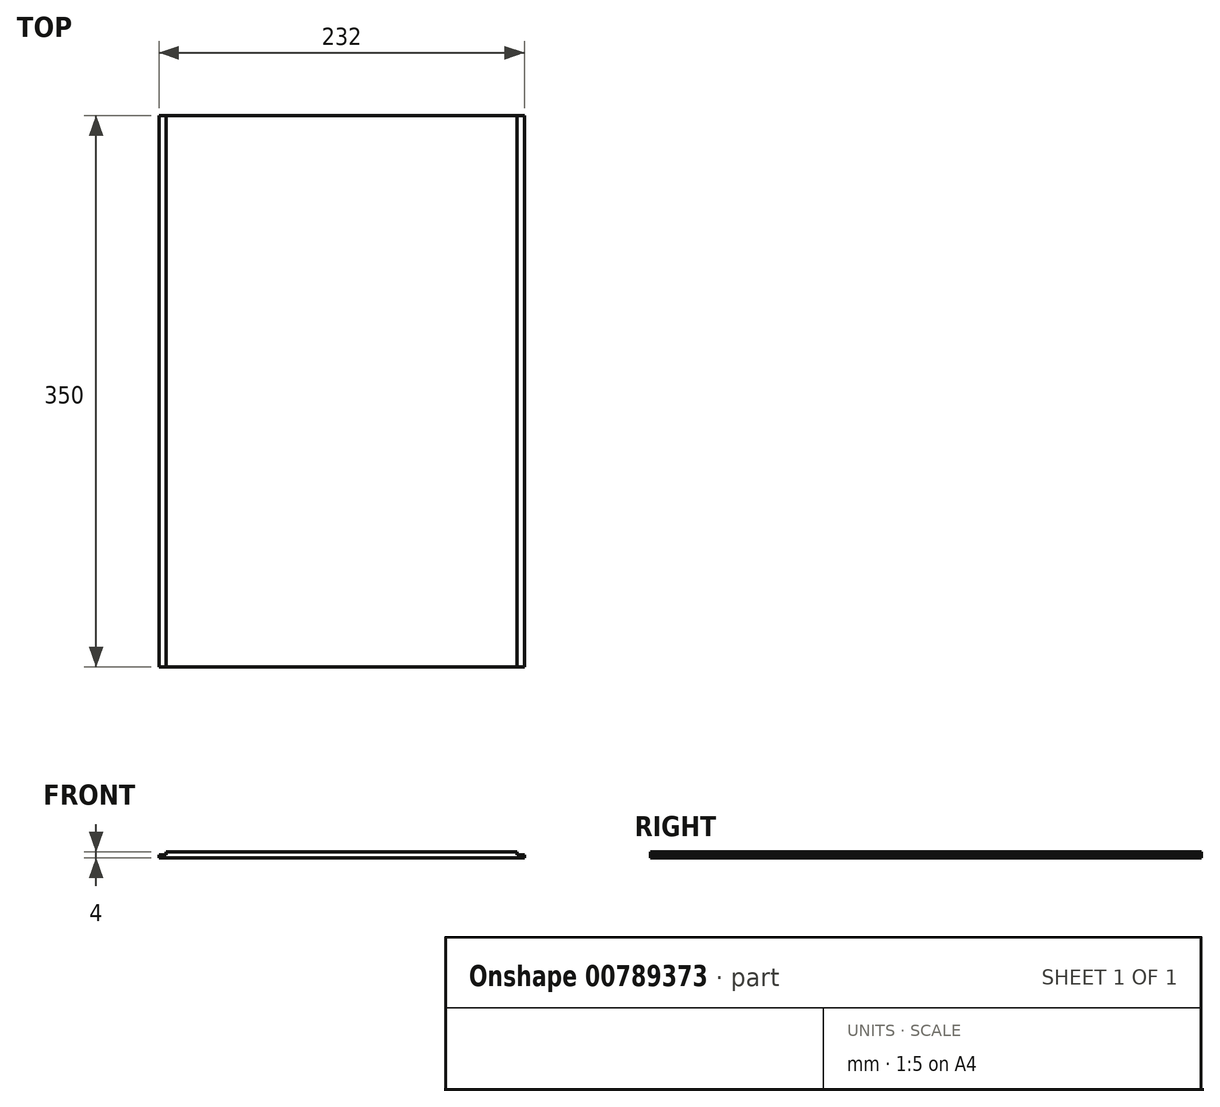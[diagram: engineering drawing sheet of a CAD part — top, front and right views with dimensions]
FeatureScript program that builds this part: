
annotation { "Feature Type Name" : "Feature", "Feature Type Description" : "" }
export const myFeature = defineFeature(function(context is Context, id is Id, definition is map)
    precondition{}
    {
        {
            var Q0;
            Q0=qCreatedBy(makeId("Front.planeOp"),FACE);
            var sketch = newSketch(context, id + "F0", { "sketchPlane" : qUnion([Q0])});
            skLineSegment(sketch, "E0", {"start": v(0, 0) * mm, "end": v(232, 0) * mm});
            skLineSegment(sketch, "E1", {"start": v(232, 0) * mm, "end": v(232, 2) * mm});
            skLineSegment(sketch, "E2", {"start": v(232, 2) * mm, "end": v(227.5, 2) * mm});
            skLineSegment(sketch, "E3", {"start": v(227.5, 2) * mm, "end": v(227.5, 4) * mm});
            skLineSegment(sketch, "E4", {"start": v(227.5, 4) * mm, "end": v(4.5, 4) * mm});
            skLineSegment(sketch, "E5", {"start": v(4.5, 4) * mm, "end": v(4.5, 2) * mm});
            skLineSegment(sketch, "E6", {"start": v(4.5, 2) * mm, "end": v(0, 2) * mm});
            skLineSegment(sketch, "E7", {"start": v(0, 2) * mm, "end": v(0, 0) * mm});
            skSolve(sketch);
        }
        {
            var Q0;
            Q0=makeQuery(id+"F0.imprint","IMPRINT",FACE,{"disambiguationData":[TD([[makeQuery(id+"F0.imprint","IMPRINT",EDGE,{"derivedFrom":sQuery(id+"F0.wireOp",EDGE,"E0")}),1.0]])]});
            extrude(context, id + "F1", {"entities" : qUnion([Q0]), "depth" : 350 * mm, "offsetDistance" : 25 * mm});
        }
    });
